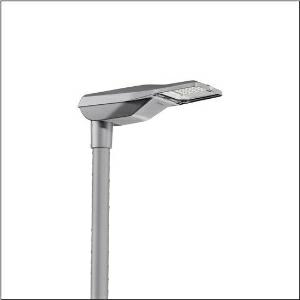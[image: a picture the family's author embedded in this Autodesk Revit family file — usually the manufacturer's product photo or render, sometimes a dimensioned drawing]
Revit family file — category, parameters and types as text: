
# Revit family: streetlight_sl_21_iq_micro___st0_8a_5xe1c21g08cb_23b1
name_source: partatom
category: Lighting Fixtures
units: mm (PartAtom-declared; Revit-internal decimal feet)

## family parameters
Cut with Voids When Loaded = No
Host = Face
Light Source = No
Part Type = Normal
Room Calculation Point = No
Round Connector Dimension = Use Diameter
Shared = No

## types (1)
- --- (1 x LED, 2380 lm, 19.4 W, 2200K)
    Apparent Load = 19 VA
    CIE Flux Codes = 38 75 97 100 100
    Color Rendering = 70
    Color Temperature = 2200K
    Default Elevation = 1800 mm
    Description = Streetlight SL 21 iQ micro, mast luminaire, primary light control with lens, of PMMA, primary optical cover: cover, of toughened safety glass, transparent, light distribution: ST0.8a, light emission: direct distribution, primary light characteristic: asymmetric, installation type: post-top, side-entry, LED, High Power LED, rated luminous flux: 2.380lm, luminous efficacy: 123lm/W, light colour: 722, colour temperature: 2200K, control gear: iQ Street-Remote, control: Street-Remote, Auto-Match, Temp-Guard, Lumen-Switch, Night-Set, Smart-Wire, Light-Fading, Desk-Remote (wireless, voltage-free reading and setting of iQ features in the workshop via application-optimized NFC function/RFID function), optimised constant luminous flux control (CLO 2.0), pre-setting: linear dimming characteristic, mains connection: 220..240V, AC, 50/60Hz, start of lifetime: 19W, end of service life: 20W, reduction: 10W, luminaire housing, of diecast aluminium, powder-coated, SITECO metallic grey (DB 702S), corrosivity category C5 high according to DIN EN ISO 12944, please order mast flange separately, inclination adjustable: 0°, 5°, 10°, 15°, sealing non-destructively replaceable, multi-level sealing system, length: 528mm, width: 235mm, height: 110mm, mast flange for spigot size: 42mm (side-entry): 5XC10008XM4, 60/48mm (side-entry/post-top): 5XC10108XM2, 76/60mm (side-entry/post-top): 5XC10108XM1, protection rating (complete): IP66, insulation class (complete): insulation class II (safety insulation), certification: CE, ENEC, ENEC+, VDE, impact resistance: IK10, permissible operating ambient temperature for outdoor applications: -40..+50°C, standard-compliant lighting for roads and squares, packaging unit: 1 piece

Light Distribution: ST0.8a
    Height = 110 mm
    Lamp = 1 x LED
    Lamp Light Flux = 2380 lm
    Lamp Power = 19.4 W
    Lamp count = 1
    Length = 528 mm
    Luminous efficacy = 123 lm/W
    Manufacturer = Siteco
    ModVariant = No
    Model = 5XE1C21G08CB
    Number of Poles = 1
    OnlyDefault = Yes
    Power Factor = 1
    Product Name = Streetlight SL 21 iQ micro | ST0.8a
    Product group = mast luminaire | pylon top
    ProductGroupID = 6100
    Protection Class = Protection class II
    Protection Degree = IP 66
    RLX_Detail_Level = 1
    RLX_Emergency_Light_Flux = 0 lm
    RLX_Emergency_Type = 0
    RLX_Emergency_Type_DB = No
    RlxData = <blob elided: 99329 chars, md5=825f6f81>
    Socket = socket
    Standby Power = 0 W
    System Light Flux = 2380 lm
    System Power = 19 W
    Type Comments = factory setting: luminous flux: 100 % | dim-lin: 254 | 387 mA
    Type Image = l_1006881.jpg
    URL = http://relux.com
    VarID = @adj_137995
    Voltage = 0 V
    Weight = 0.00 kg
    Width = 235 mm

## geometry (parser evidence)
native form markers: Blend x4, Sweep x10
no freeform markers — native parametric forms only
